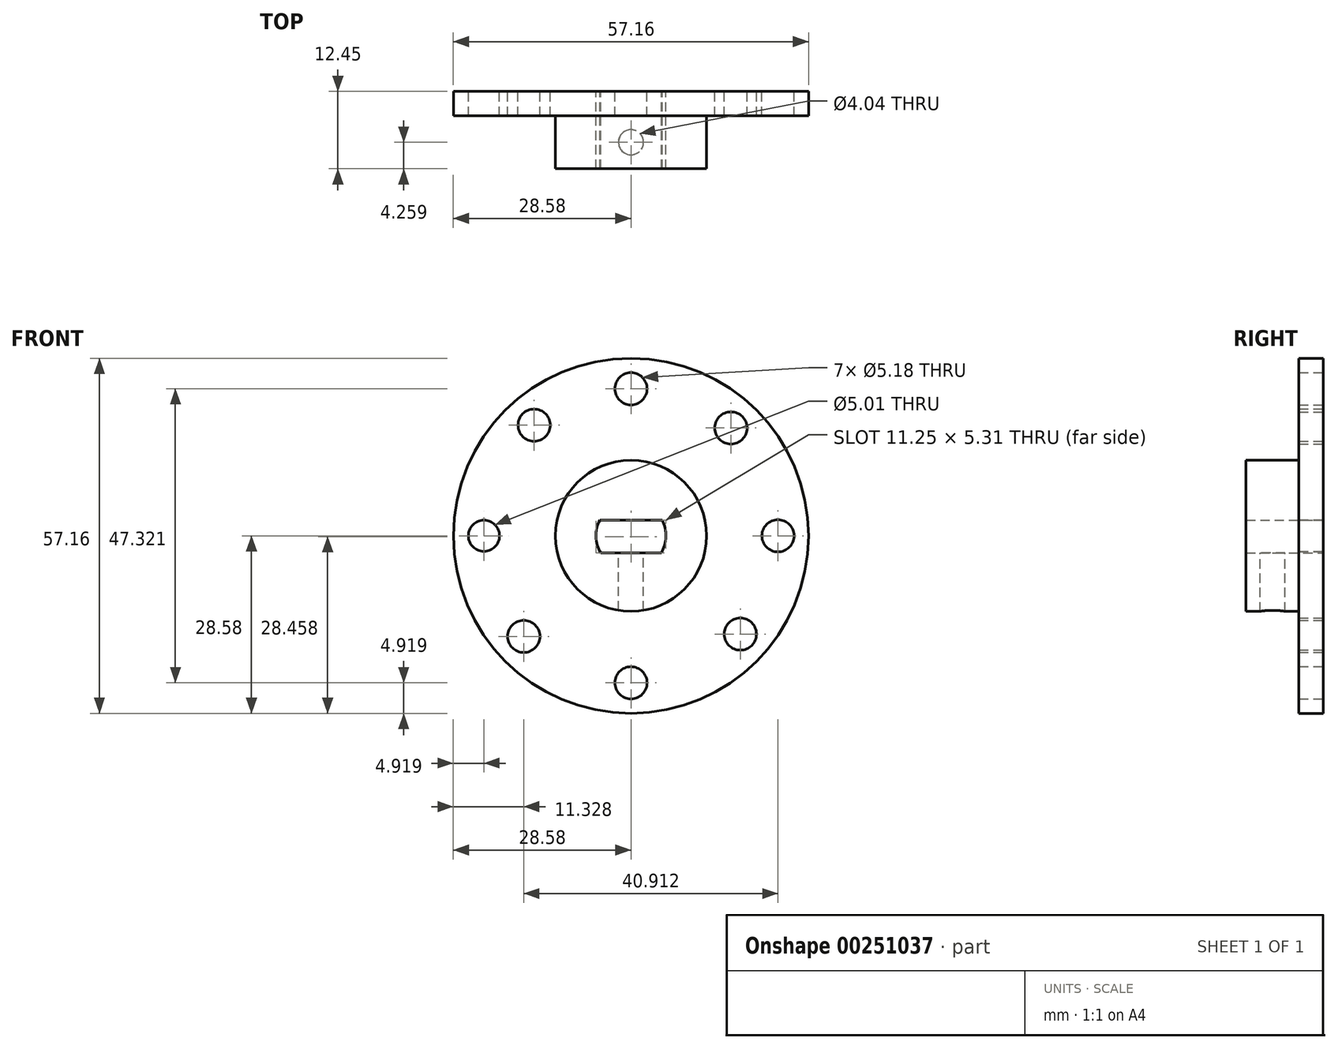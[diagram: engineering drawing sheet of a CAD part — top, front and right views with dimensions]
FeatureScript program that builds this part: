
annotation { "Feature Type Name" : "Feature", "Feature Type Description" : "" }
export const myFeature = defineFeature(function(context is Context, id is Id, definition is map)
    precondition{}
    {
        {
            var Q0;
            Q0=qCreatedBy(makeId("Front.planeOp"),FACE);
            var sketch = newSketch(context, id + "F0", { "sketchPlane" : qUnion([Q0])});
            skCircle(sketch, "E0", {"center": v(0, 0) * mm, "radius": 28.58 * mm});
            skArc(sketch, "E1", {"start": v(-5.02, 2.53) * mm, "mid": v(-5.62, -0.14) * mm, "end": v(-4.9, -2.78) * mm});
            skLineSegment(sketch, "E2", {"start": v(-5.02, 2.53) * mm, "end": v(5.02, 2.53) * mm});
            skLineSegment(sketch, "E3", {"start": v(-4.9, -2.78) * mm, "end": v(4.9, -2.78) * mm});
            skCircle(sketch, "E4", {"center": v(-15.59, 17.8) * mm, "radius": 2.6 * mm});
            skCircle(sketch, "E5", {"center": v(-23.66, 0) * mm, "radius": 2.5 * mm});
            skCircle(sketch, "E6", {"center": v(-17.25, -16.2) * mm, "radius": 2.6 * mm});
            skCircle(sketch, "E7", {"center": v(0, -23.66) * mm, "radius": 2.6 * mm});
            skCircle(sketch, "E8", {"center": v(17.6, -15.82) * mm, "radius": 2.6 * mm});
            skCircle(sketch, "E9", {"center": v(23.66, 0) * mm, "radius": 2.6 * mm});
            skCircle(sketch, "E10", {"center": v(16.09, 17.35) * mm, "radius": 2.6 * mm});
            skCircle(sketch, "E11", {"center": v(0, 23.66) * mm, "radius": 2.6 * mm});
            skArc(sketch, "E12.trimOffspring", {"start": v(4.9, -2.78) * mm, "mid": v(5.62, -0.14) * mm, "end": v(5.02, 2.53) * mm});
            skCircle(sketch, "E13", {"center": v(0, 0) * mm, "radius": 12.17 * mm});
            skSolve(sketch);
        }
        {
            var Q0;
            Q0=makeQuery(id+"F0.imprint","IMPRINT",FACE,{"disambiguationData":[TD([[makeQuery(id+"F0.imprint","IMPRINT",EDGE,{"derivedFrom":sQuery(id+"F0.wireOp",EDGE,"E1")}),-1.0]])]});
            extrude(context, id + "F1", {"entities" : qUnion([Q0]), "depth" : 12.45 * mm});
        }
        {
            var Q0;
            Q0 = qSketchRegion(id + "F0", true);
            extrude(context, id + "F2", {"entities" : qUnion([Q0]), "operationType" : NewBodyOperationType.ADD, "depth" : 3.94 * mm});
        }
        {
            var Q0;
            Q0=qCreatedBy(makeId("Top.planeOp"),FACE);
            var sketch = newSketch(context, id + "F3", { "sketchPlane" : qUnion([Q0])});
            skCircle(sketch, "E14", {"center": v(0, -8.2) * mm, "radius": 2.02 * mm});
            skSolve(sketch);
        }
        {
            var Q0;
            Q0 = qSketchRegion(id + "F3", true);
            extrude(context, id + "F4", {"entities" : qUnion([Q0]), "operationType" : NewBodyOperationType.REMOVE, "oppositeDirection" : true, "depth" : 25.4 * mm});
        }
    });
